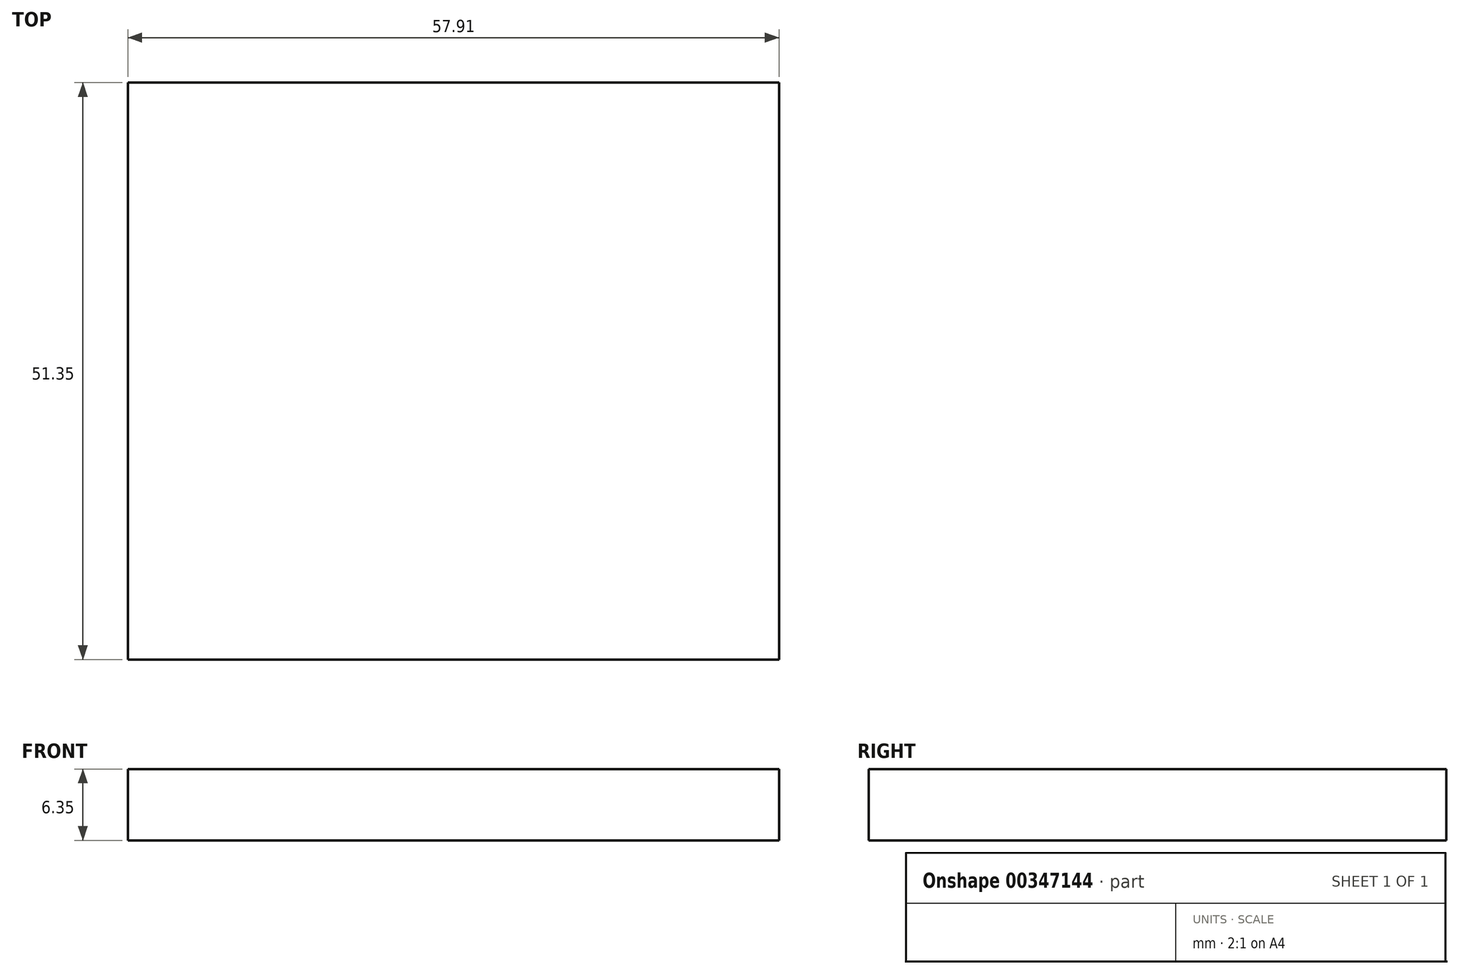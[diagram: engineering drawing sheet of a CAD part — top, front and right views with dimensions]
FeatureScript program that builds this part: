
annotation { "Feature Type Name" : "Feature", "Feature Type Description" : "" }
export const myFeature = defineFeature(function(context is Context, id is Id, definition is map)
    precondition{}
    {
        {
            var Q0;
            Q0=qCreatedBy(makeId("Top.planeOp"),FACE);
            var sketch = newSketch(context, id + "F0", { "sketchPlane" : qUnion([Q0])});
            skLineSegment(sketch, "E0.bottom", {"start": v(0, 0) * mm, "end": v(-57.9, 0) * mm});
            skLineSegment(sketch, "E0.top", {"start": v(0, -51.35) * mm, "end": v(-57.9, -51.35) * mm});
            skLineSegment(sketch, "E0.left", {"start": v(0, 0) * mm, "end": v(0, -51.35) * mm});
            skLineSegment(sketch, "E0.right", {"start": v(-57.9, 0) * mm, "end": v(-57.9, -51.35) * mm});
            skSolve(sketch);
        }
        {
            var Q0;
            Q0=makeQuery(id+"F0.imprint","IMPRINT",FACE,{"disambiguationData":[TD([[makeQuery(id+"F0.imprint","IMPRINT",EDGE,{"derivedFrom":sQuery(id+"F0.wireOp",EDGE,"E0.bottom")}),1.0]])]});
            extrude(context, id + "F1", {"entities" : qUnion([Q0]), "depth" : 6.35 * mm});
        }
    });
